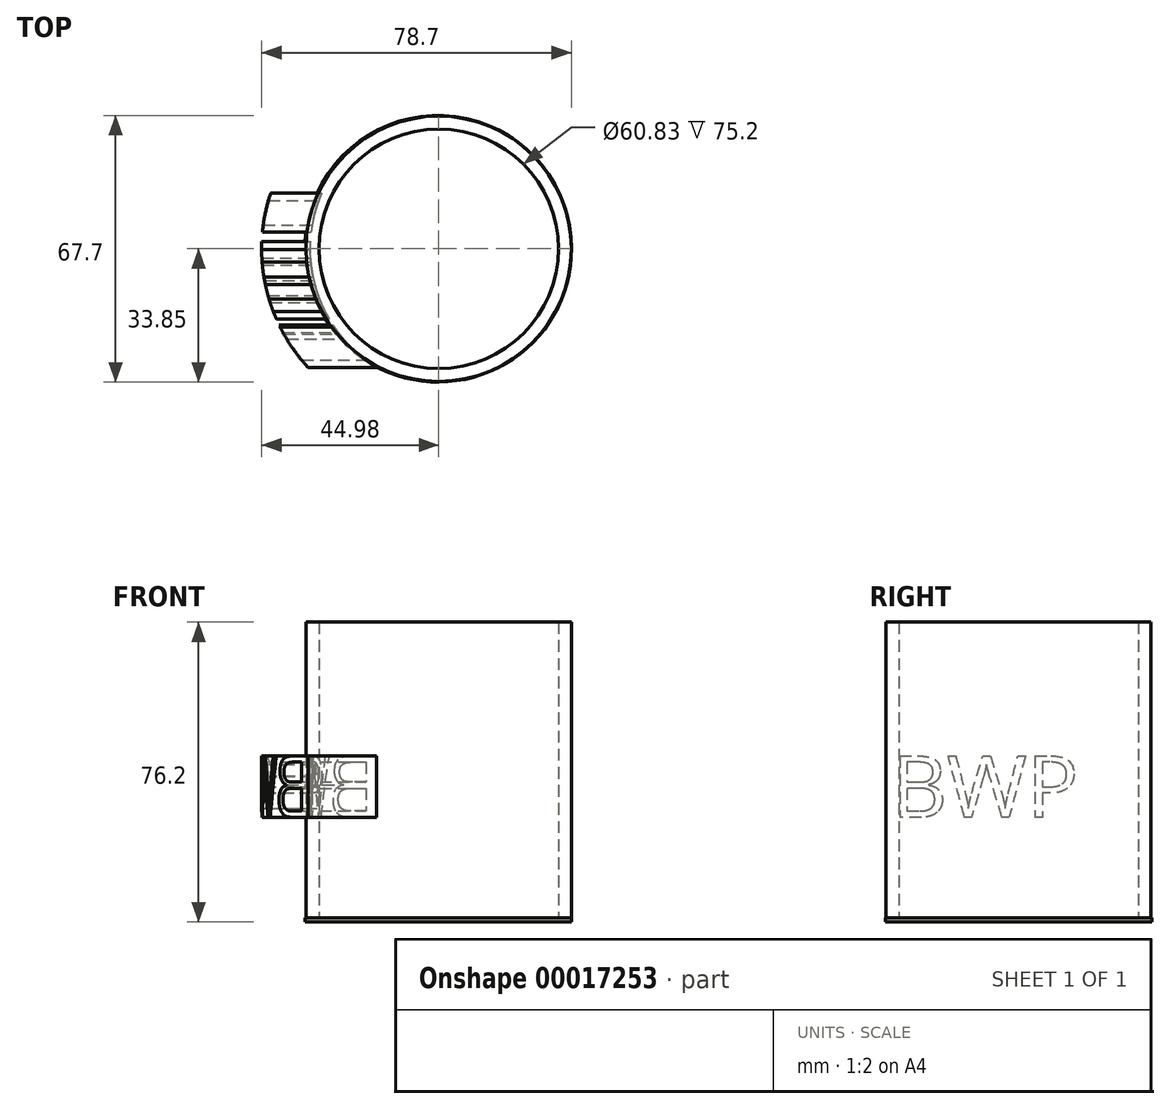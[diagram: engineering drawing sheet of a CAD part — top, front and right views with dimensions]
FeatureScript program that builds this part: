
annotation { "Feature Type Name" : "Feature", "Feature Type Description" : "" }
export const myFeature = defineFeature(function(context is Context, id is Id, definition is map)
    precondition{}
    {
        {
            var Q0;
            Q0=qCreatedBy(makeId("Top.planeOp"),FACE);
            var sketch = newSketch(context, id + "F0", { "sketchPlane" : qUnion([Q0])});
            skCircle(sketch, "E0", {"center": v(43.47, 0) * mm, "radius": 44.45 * mm});
            skSolve(sketch);
        }
        {
            var Q0;
            Q0=makeQuery(id+"F0.imprint","IMPRINT",FACE,{"disambiguationData":[TD([[makeQuery(id+"F0.imprint","IMPRINT",EDGE,{"derivedFrom":sQuery(id+"F0.wireOp",EDGE,"E0")}),1.0]])]});
            extrude(context, id + "F1", {"entities" : qUnion([Q0]), "depth" : 127 * mm});
        }
        {
            var Q0;
            Q0=qCreatedBy(makeId("Top.planeOp"),FACE);
            var sketch = newSketch(context, id + "F2", { "sketchPlane" : qUnion([Q0])});
            skCircle(sketch, "E1", {"center": v(46.64, 0) * mm, "radius": 35.3 * mm});
            skSolve(sketch);
        }
        {
            var Q0;
            Q0=makeQuery(id+"F2.imprint","IMPRINT",FACE,{"disambiguationData":[TD([[makeQuery(id+"F2.imprint","IMPRINT",EDGE,{"derivedFrom":sQuery(id+"F2.wireOp",EDGE,"E1")}),1.0]])]});
            extrude(context, id + "F3", {"entities" : qUnion([Q0]), "operationType" : NewBodyOperationType.REMOVE, "depth" : 114.33 * mm});
        }
        {
            var Q0;
            Q0=qCreatedBy(makeId("Right.planeOp"),FACE);
            var sketch = newSketch(context, id + "F4", { "sketchPlane" : qUnion([Q0])});
            skText(sketch, "E2", { "text": "BWP", "fontName": "OpenSans-Regular.ttf"});
            const initialGuessF4  = {"E2": [-0.03227, 0.02662, 1, 0, 0.01571]};
            skSetInitialGuess(sketch, initialGuessF4);
            skSolve(sketch);
        }
        {
            var Q0;
            Q0=makeQuery(id+"F4.imprint","IMPRINT",FACE,{"disambiguationData":[TD([[makeQuery(id+"F4.imprint","IMPRINT",EDGE,{"derivedFrom":sQuery(id+"F4.wireOp",EDGE,"E2.sketch_text.stroke-45")}),-1.0]])]});
            var Q1;
            Q1=makeQuery(id+"F4.imprint","IMPRINT",FACE,{"disambiguationData":[TD([[makeQuery(id+"F4.imprint","IMPRINT",EDGE,{"derivedFrom":sQuery(id+"F4.wireOp",EDGE,"E2.sketch_text.stroke-25")}),-1.0]])]});
            var Q2;
            Q2=makeQuery(id+"F4.imprint","IMPRINT",FACE,{"disambiguationData":[TD([[makeQuery(id+"F4.imprint","IMPRINT",EDGE,{"derivedFrom":sQuery(id+"F4.wireOp",EDGE,"E2.sketch_text.stroke-0")}),-1.0]])]});
            extrude(context, id + "F5", {"entities" : qUnion([Q0, Q1, Q2]), "operationType" : NewBodyOperationType.INTERSECT, "oppositeDirection" : true, "depth" : 19.88 * mm, "hasSecondDirection" : true, "secondDirectionOppositeDirection" : false, "secondDirectionDepth" : 32.97 * mm});
        }
        {
            var Q0;
            Q0=qCreatedBy(makeId("Top.planeOp"),FACE);
            var sketch = newSketch(context, id + "F6", { "sketchPlane" : qUnion([Q0])});
            skCircle(sketch, "E3", {"center": v(44, 0) * mm, "radius": 33.68 * mm});
            skCircle(sketch, "E4", {"center": v(44, 0) * mm, "radius": 30.42 * mm});
            skSolve(sketch);
        }
        {
            var Q0;
            Q0=makeQuery(id+"F6.imprint","IMPRINT",FACE,{"disambiguationData":[TD([[makeQuery(id+"F6.imprint","IMPRINT",EDGE,{"derivedFrom":sQuery(id+"F6.wireOp",EDGE,"E3")}),1.0]])]});
            extrude(context, id + "F7", {"entities" : qUnion([Q0]), "depth" : 76.2 * mm});
        }
        {
            var Q0;
            Q0=qCreatedBy(makeId("Top.planeOp"),FACE);
            var sketch = newSketch(context, id + "F8", { "sketchPlane" : qUnion([Q0])});
            skCircle(sketch, "E5", {"center": v(43.87, 0) * mm, "radius": 33.85 * mm});
            skSolve(sketch);
        }
        {
            var Q0;
            Q0=makeQuery(id+"F8.imprint","IMPRINT",FACE,{"disambiguationData":[TD([[makeQuery(id+"F8.imprint","IMPRINT",EDGE,{"derivedFrom":sQuery(id+"F8.wireOp",EDGE,"E5")}),1.0]])]});
            extrude(context, id + "F9", {"entities" : qUnion([Q0]), "operationType" : NewBodyOperationType.ADD, "depth" : 1 * mm});
        }
    });
